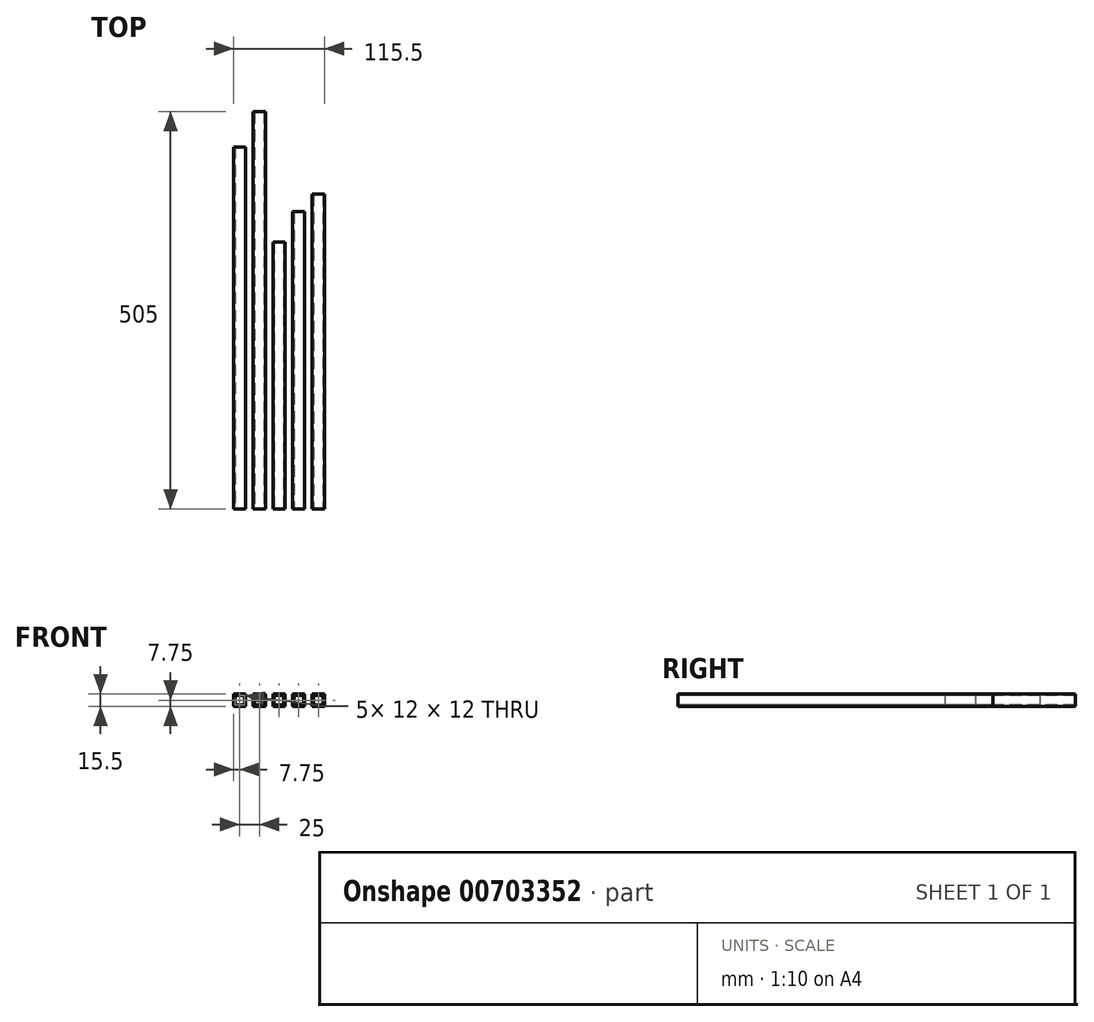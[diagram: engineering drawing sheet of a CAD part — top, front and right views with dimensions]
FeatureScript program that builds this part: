
annotation { "Feature Type Name" : "Feature", "Feature Type Description" : "" }
export const myFeature = defineFeature(function(context is Context, id is Id, definition is map)
    precondition{}
    {
        {
            var Q0;
            Q0=qCreatedBy(makeId("Front.planeOp"),FACE);
            var sketch = newSketch(context, id + "F0", { "sketchPlane" : qUnion([Q0])});
            skLineSegment(sketch, "E0.bottom", {"start": v(-17.75, 7.75) * mm, "end": v(-2.25, 7.75) * mm});
            skLineSegment(sketch, "E0.top", {"start": v(-17.75, -7.75) * mm, "end": v(-2.25, -7.75) * mm});
            skLineSegment(sketch, "E0.left", {"start": v(-17.75, 7.75) * mm, "end": v(-17.75, -7.75) * mm});
            skLineSegment(sketch, "E0.right", {"start": v(-2.25, 7.75) * mm, "end": v(-2.25, -7.75) * mm});
            skPoint(sketch, "E0.middle", {"position": v(-10, 0) * mm});
            skLineSegment(sketch, "E1.bottom", {"start": v(-16, 6) * mm, "end": v(-4, 6) * mm});
            skLineSegment(sketch, "E1.top", {"start": v(-16, -6) * mm, "end": v(-4, -6) * mm});
            skLineSegment(sketch, "E1.left", {"start": v(-16, 6) * mm, "end": v(-16, -6) * mm});
            skLineSegment(sketch, "E1.right", {"start": v(-4, 6) * mm, "end": v(-4, -6) * mm});
            skLineSegment(sketch, "E2.1.0.0", {"start": v(7.25, 7.75) * mm, "end": v(22.75, 7.75) * mm});
            skLineSegment(sketch, "E2.1.0.1", {"start": v(7.25, -7.75) * mm, "end": v(22.75, -7.75) * mm});
            skLineSegment(sketch, "E2.1.0.2", {"start": v(7.25, 7.75) * mm, "end": v(7.25, -7.75) * mm});
            skLineSegment(sketch, "E2.1.0.3", {"start": v(22.75, 7.75) * mm, "end": v(22.75, -7.75) * mm});
            skLineSegment(sketch, "E2.1.0.4", {"start": v(9, 6) * mm, "end": v(21, 6) * mm});
            skLineSegment(sketch, "E2.1.0.5", {"start": v(9, -6) * mm, "end": v(21, -6) * mm});
            skPoint(sketch, "E2.1.0.6", {"position": v(15, 0) * mm});
            skLineSegment(sketch, "E2.1.0.7", {"start": v(9, 6) * mm, "end": v(9, -6) * mm});
            skLineSegment(sketch, "E2.1.0.8", {"start": v(21, 6) * mm, "end": v(21, -6) * mm});
            skPoint(sketch, "E2.1.0.9", {"position": v(15, 0) * mm});
            skLineSegment(sketch, "E2.direction1", {"start": v(-17.75, -7.75) * mm, "end": v(7.25, -7.75) * mm, "construction": true});
            skLineSegment(sketch, "E3.0.2.0", {"start": v(32.25, 7.75) * mm, "end": v(47.75, 7.75) * mm});
            skLineSegment(sketch, "E3.3.2.0", {"start": v(32.25, -7.75) * mm, "end": v(47.75, -7.75) * mm});
            skLineSegment(sketch, "E3.6.2.0", {"start": v(32.25, 7.75) * mm, "end": v(32.25, -7.75) * mm});
            skLineSegment(sketch, "E3.9.2.0", {"start": v(47.75, 7.75) * mm, "end": v(47.75, -7.75) * mm});
            skLineSegment(sketch, "E3.12.2.0", {"start": v(34, 6) * mm, "end": v(46, 6) * mm});
            skLineSegment(sketch, "E3.15.2.0", {"start": v(34, -6) * mm, "end": v(46, -6) * mm});
            skPoint(sketch, "E3.18.2.0", {"position": v(40, 0) * mm});
            skLineSegment(sketch, "E3.19.2.0", {"start": v(34, 6) * mm, "end": v(34, -6) * mm});
            skLineSegment(sketch, "E3.22.2.0", {"start": v(46, 6) * mm, "end": v(46, -6) * mm});
            skPoint(sketch, "E3.25.2.0", {"position": v(40, 0) * mm});
            skLineSegment(sketch, "E4.0.3.0", {"start": v(57.25, 7.75) * mm, "end": v(72.75, 7.75) * mm});
            skLineSegment(sketch, "E4.3.3.0", {"start": v(57.25, -7.75) * mm, "end": v(72.75, -7.75) * mm});
            skLineSegment(sketch, "E4.6.3.0", {"start": v(57.25, 7.75) * mm, "end": v(57.25, -7.75) * mm});
            skLineSegment(sketch, "E4.9.3.0", {"start": v(72.75, 7.75) * mm, "end": v(72.75, -7.75) * mm});
            skLineSegment(sketch, "E4.12.3.0", {"start": v(59, 6) * mm, "end": v(71, 6) * mm});
            skLineSegment(sketch, "E4.15.3.0", {"start": v(59, -6) * mm, "end": v(71, -6) * mm});
            skPoint(sketch, "E4.18.3.0", {"position": v(65, 0) * mm});
            skLineSegment(sketch, "E4.19.3.0", {"start": v(59, 6) * mm, "end": v(59, -6) * mm});
            skLineSegment(sketch, "E4.22.3.0", {"start": v(71, 6) * mm, "end": v(71, -6) * mm});
            skPoint(sketch, "E4.25.3.0", {"position": v(65, 0) * mm});
            skLineSegment(sketch, "E5.0.4.0", {"start": v(82.25, 7.75) * mm, "end": v(97.75, 7.75) * mm});
            skLineSegment(sketch, "E5.3.4.0", {"start": v(82.25, -7.75) * mm, "end": v(97.75, -7.75) * mm});
            skLineSegment(sketch, "E5.6.4.0", {"start": v(82.25, 7.75) * mm, "end": v(82.25, -7.75) * mm});
            skLineSegment(sketch, "E5.9.4.0", {"start": v(97.75, 7.75) * mm, "end": v(97.75, -7.75) * mm});
            skLineSegment(sketch, "E5.12.4.0", {"start": v(84, 6) * mm, "end": v(96, 6) * mm});
            skLineSegment(sketch, "E5.15.4.0", {"start": v(84, -6) * mm, "end": v(96, -6) * mm});
            skPoint(sketch, "E5.18.4.0", {"position": v(90, 0) * mm});
            skLineSegment(sketch, "E5.19.4.0", {"start": v(84, 6) * mm, "end": v(84, -6) * mm});
            skLineSegment(sketch, "E5.22.4.0", {"start": v(96, 6) * mm, "end": v(96, -6) * mm});
            skPoint(sketch, "E5.25.4.0", {"position": v(90, 0) * mm});
            skSolve(sketch);
        }
        {
            var Q0;
            Q0=makeQuery(id+"F0.imprint","IMPRINT",FACE,{"disambiguationData":[TD([[makeQuery(id+"F0.imprint","IMPRINT",EDGE,{"derivedFrom":sQuery(id+"F0.wireOp",EDGE,"E0.bottom")}),-1.0]])]});
            extrude(context, id + "F1", {"entities" : qUnion([Q0]), "oppositeDirection" : true, "depth" : 460 * mm, "offsetDistance" : 25 * mm});
        }
        {
            var Q0;
            Q0=makeQuery(id+"F0.imprint","IMPRINT",FACE,{"disambiguationData":[TD([[makeQuery(id+"F0.imprint","IMPRINT",EDGE,{"derivedFrom":sQuery(id+"F0.wireOp",EDGE,"E2.1.0.0")}),-1.0]])]});
            extrude(context, id + "F2", {"entities" : qUnion([Q0]), "oppositeDirection" : true, "depth" : 505 * mm, "offsetDistance" : 25 * mm});
        }
        {
            var Q0;
            Q0=makeQuery(id+"F0.imprint","IMPRINT",FACE,{"disambiguationData":[TD([[makeQuery(id+"F0.imprint","IMPRINT",EDGE,{"derivedFrom":sQuery(id+"F0.wireOp",EDGE,"E3.0.2.0")}),-1.0]])]});
            extrude(context, id + "F3", {"entities" : qUnion([Q0]), "oppositeDirection" : true, "depth" : 339 * mm, "offsetDistance" : 25 * mm});
        }
        {
            var Q0;
            Q0=makeQuery(id+"F0.imprint","IMPRINT",FACE,{"disambiguationData":[TD([[makeQuery(id+"F0.imprint","IMPRINT",EDGE,{"derivedFrom":sQuery(id+"F0.wireOp",EDGE,"E4.0.3.0")}),-1.0]])]});
            extrude(context, id + "F4", {"entities" : qUnion([Q0]), "oppositeDirection" : true, "depth" : 377.75 * mm, "offsetDistance" : 25 * mm});
        }
        {
            var Q0;
            Q0=makeQuery(id+"F0.imprint","IMPRINT",FACE,{"disambiguationData":[TD([[makeQuery(id+"F0.imprint","IMPRINT",EDGE,{"derivedFrom":sQuery(id+"F0.wireOp",EDGE,"E5.0.4.0")}),-1.0]])]});
            extrude(context, id + "F5", {"entities" : qUnion([Q0]), "oppositeDirection" : true, "depth" : 400 * mm, "offsetDistance" : 25 * mm});
        }
    });
